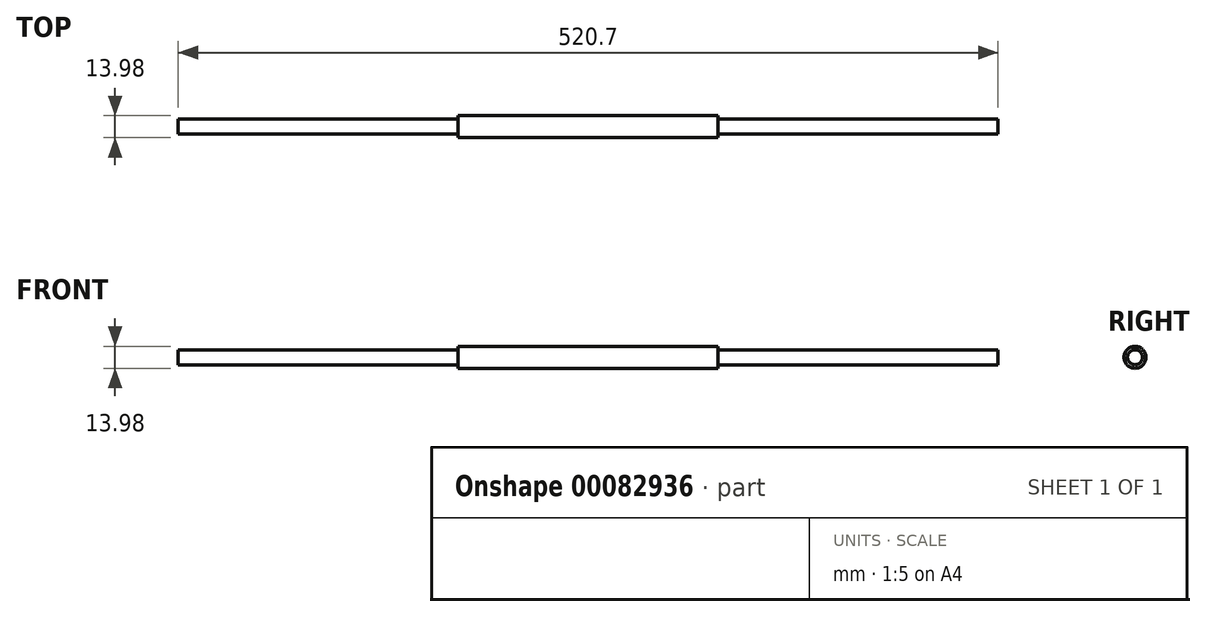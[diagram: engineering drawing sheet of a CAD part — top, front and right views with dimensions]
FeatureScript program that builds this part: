
annotation { "Feature Type Name" : "Feature", "Feature Type Description" : "" }
export const myFeature = defineFeature(function(context is Context, id is Id, definition is map)
    precondition{}
    {
        {
            var Q0;
            Q0=qCreatedBy(makeId("Front.planeOp"),FACE);
            var sketch = newSketch(context, id + "F0", { "sketchPlane" : qUnion([Q0])});
            skLineSegment(sketch, "E0.bottom", {"start": v(-82.55, 6.99) * mm, "end": v(82.55, 6.99) * mm});
            skLineSegment(sketch, "E0.top", {"start": v(-82.55, -6.99) * mm, "end": v(82.55, -6.99) * mm});
            skLineSegment(sketch, "E0.left", {"start": v(-82.55, 6.99) * mm, "end": v(-82.55, -6.98) * mm});
            skLineSegment(sketch, "E0.right", {"start": v(82.55, 6.99) * mm, "end": v(82.55, -6.98) * mm});
            skPoint(sketch, "E0.middle", {"position": v(0, 0) * mm});
            skLineSegment(sketch, "E1.bottom", {"start": v(-260.35, 4.76) * mm, "end": v(260.35, 4.76) * mm});
            skLineSegment(sketch, "E1.top", {"start": v(-260.35, -4.76) * mm, "end": v(260.35, -4.76) * mm});
            skLineSegment(sketch, "E1.left", {"start": v(-260.35, 4.76) * mm, "end": v(-260.35, -4.76) * mm});
            skLineSegment(sketch, "E1.right", {"start": v(260.35, 4.76) * mm, "end": v(260.35, -4.76) * mm});
            skLineSegment(sketch, "E2", {"start": v(-260.35, 0) * mm, "end": v(260.35, 0) * mm, "construction": true});
            skLineSegment(sketch, "E3", {"start": v(-260.35, 0) * mm, "end": v(260.35, 0) * mm});
            skSolve(sketch);
        }
        {
            var Q0;
            {var subQ0=sQuery(id+"F0.wireOp",EDGE,"E1.bottom");var subQ1=sQuery(id+"F0.wireOp",EDGE,"E0.left");var subQ2=makeQuery(id+"F0.imprint","INTERSECT",VERTEX,{"derivedFrom":[subQ1,subQ0]});Q0=makeQuery(id+"F0.imprint","IMPRINT",FACE,{"disambiguationData":[TD([[makeQuery(id+"F0.imprint","IMPRINT",EDGE,{"disambiguationData":[TD([[subQ2,-1.0]])],"derivedFrom":subQ1}),-1.0]])]});}
            var Q1;
            {var subQ0=sQuery(id+"F0.wireOp",EDGE,"E0.bottom");Q1=makeQuery(id+"F0.imprint","IMPRINT",FACE,{"disambiguationData":[TD([[makeQuery(id+"F0.imprint","IMPRINT",EDGE,{"derivedFrom":subQ0}),-1.0]])]});}
            var Q2;
            {var subQ0=sQuery(id+"F0.wireOp",EDGE,"E1.bottom");var subQ1=sQuery(id+"F0.wireOp",EDGE,"E0.left");var subQ2=makeQuery(id+"F0.imprint","INTERSECT",VERTEX,{"derivedFrom":[subQ1,subQ0]});Q2=makeQuery(id+"F0.imprint","IMPRINT",FACE,{"disambiguationData":[TD([[makeQuery(id+"F0.imprint","IMPRINT",EDGE,{"disambiguationData":[TD([[subQ2,-1.0]])],"derivedFrom":subQ1}),1.0]])]});}
            var Q3;
            {var subQ0=sQuery(id+"F0.wireOp",EDGE,"E1.bottom");var subQ1=sQuery(id+"F0.wireOp",EDGE,"E0.right");var subQ2=makeQuery(id+"F0.imprint","INTERSECT",VERTEX,{"derivedFrom":[subQ1,subQ0]});Q3=makeQuery(id+"F0.imprint","IMPRINT",FACE,{"disambiguationData":[TD([[makeQuery(id+"F0.imprint","IMPRINT",EDGE,{"disambiguationData":[TD([[subQ2,-1.0]])],"derivedFrom":subQ1}),1.0]])]});}
            var Q4;
            Q4=sQuery(id+"F0.wireOp",EDGE,"E3");
            revolve(context, id + "F1", {"entities" : qUnion([Q0, Q1, Q2, Q3]), "axis" : qUnion([Q4]), "revolveType" : RevolveType.FULL});
        }
    });
